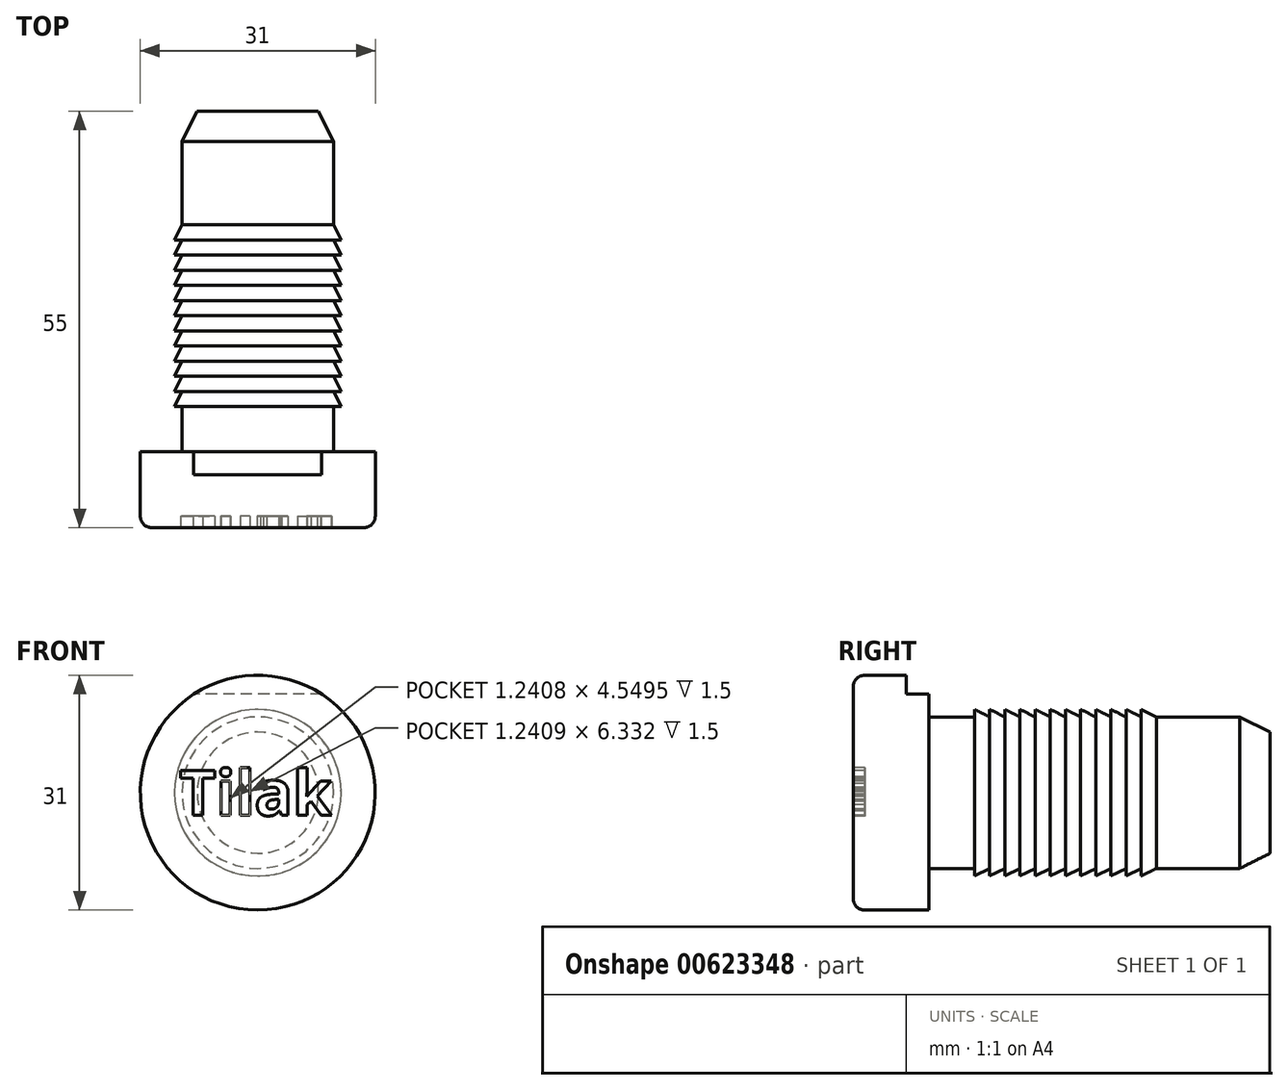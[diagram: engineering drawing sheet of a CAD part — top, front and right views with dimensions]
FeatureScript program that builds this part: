
annotation { "Feature Type Name" : "Feature", "Feature Type Description" : "" }
export const myFeature = defineFeature(function(context is Context, id is Id, definition is map)
    precondition{}
    {
        {
            var Q0;
            Q0=qCreatedBy(makeId("Front.planeOp"),FACE);
            var sketch = newSketch(context, id + "F0", { "sketchPlane" : qUnion([Q0])});
            skCircle(sketch, "E0", {"center": v(0, 0) * mm, "radius": 10 * mm});
            skSolve(sketch);
        }
        {
            var Q0;
            Q0 = qSketchRegion(id + "F0", true);
            extrude(context, id + "F1", {"entities" : qUnion([Q0]), "oppositeDirection" : true, "depth" : 45 * mm, "offsetDistance" : 25 * mm});
        }
        {
            var Q0;
            Q0=makeQuery(id+"F1.opExtrude","CAP_FACE",FACE,{"disambiguationData":[OSD([sQuery(id+"F0.wireOp",EDGE,"E0")])],"isStart":true});
            var sketch = newSketch(context, id + "F2", { "sketchPlane" : qUnion([Q0])});
            skCircle(sketch, "E1", {"center": v(0, 0) * mm, "radius": 15.5 * mm});
            skSolve(sketch);
        }
        {
            var Q0;
            Q0 = qSketchRegion(id + "F2", true);
            extrude(context, id + "F3", {"entities" : qUnion([Q0]), "operationType" : NewBodyOperationType.ADD, "depth" : 10 * mm, "offsetDistance" : 25 * mm});
        }
        {
            var Q0;
            Q0=makeQuery(id+"F3.opExtrude","CAP_FACE",FACE,{"disambiguationData":[OSD([sQuery(id+"F2.wireOp",EDGE,"E1")])],"isStart":true});
            var sketch = newSketch(context, id + "F4", { "sketchPlane" : qUnion([Q0])});
            skLineSegment(sketch, "E2", {"start": v(-8.44, 13) * mm, "end": v(8.44, 13) * mm});
            skCircle(sketch, "E3", {"center": v(0, 0) * mm, "radius": 10 * mm, "construction": true});
            skArc(sketch, "E4", {"start": v(-8.44, 13) * mm, "mid": v(0, 15.5) * mm, "end": v(8.44, 13) * mm});
            skSolve(sketch);
        }
        {
            var Q0;
            Q0 = qSketchRegion(id + "F4", true);
            extrude(context, id + "F5", {"entities" : qUnion([Q0]), "operationType" : NewBodyOperationType.REMOVE, "oppositeDirection" : true, "depth" : 3 * mm, "offsetDistance" : 25 * mm});
        }
        {
            var Q0;
            Q0=qCreatedBy(makeId("Right.planeOp"),FACE);
            var sketch = newSketch(context, id + "F6", { "sketchPlane" : qUnion([Q0])});
            skLineSegment(sketch, "E5.0", {"start": v(45, -10) * mm, "end": v(45, 10) * mm, "construction": true});
            skLineSegment(sketch, "E6", {"start": v(58.9, 0) * mm, "end": v(-32.08, 0) * mm, "construction": true});
            skLineSegment(sketch, "E7", {"start": v(30, 10) * mm, "end": v(28, 11) * mm});
            skLineSegment(sketch, "E8", {"start": v(28, 11) * mm, "end": v(28, 10) * mm});
            skLineSegment(sketch, "E9", {"start": v(28, 10) * mm, "end": v(30, 10) * mm});
            skLineSegment(sketch, "E10.0", {"start": v(0, -10) * mm, "end": v(0, 10) * mm, "construction": true});
            skLineSegment(sketch, "E11.1.0.0", {"start": v(26, 10) * mm, "end": v(28, 10) * mm});
            skLineSegment(sketch, "E11.1.0.1", {"start": v(26, 11) * mm, "end": v(26, 10) * mm});
            skLineSegment(sketch, "E11.1.0.2", {"start": v(28, 10) * mm, "end": v(26, 11) * mm});
            skLineSegment(sketch, "E11.2.0.0", {"start": v(24, 10) * mm, "end": v(26, 10) * mm});
            skLineSegment(sketch, "E11.2.0.1", {"start": v(24, 11) * mm, "end": v(24, 10) * mm});
            skLineSegment(sketch, "E11.2.0.2", {"start": v(26, 10) * mm, "end": v(24, 11) * mm});
            skLineSegment(sketch, "E11.3.0.0", {"start": v(22, 10) * mm, "end": v(24, 10) * mm});
            skLineSegment(sketch, "E11.3.0.1", {"start": v(22, 11) * mm, "end": v(22, 10) * mm});
            skLineSegment(sketch, "E11.3.0.2", {"start": v(24, 10) * mm, "end": v(22, 11) * mm});
            skLineSegment(sketch, "E11.4.0.0", {"start": v(20, 10) * mm, "end": v(22, 10) * mm});
            skLineSegment(sketch, "E11.4.0.1", {"start": v(20, 11) * mm, "end": v(20, 10) * mm});
            skLineSegment(sketch, "E11.4.0.2", {"start": v(22, 10) * mm, "end": v(20, 11) * mm});
            skLineSegment(sketch, "E11.5.0.0", {"start": v(18, 10) * mm, "end": v(20, 10) * mm});
            skLineSegment(sketch, "E11.5.0.1", {"start": v(18, 11) * mm, "end": v(18, 10) * mm});
            skLineSegment(sketch, "E11.5.0.2", {"start": v(20, 10) * mm, "end": v(18, 11) * mm});
            skLineSegment(sketch, "E11.6.0.0", {"start": v(16, 10) * mm, "end": v(18, 10) * mm});
            skLineSegment(sketch, "E11.6.0.1", {"start": v(16, 11) * mm, "end": v(16, 10) * mm});
            skLineSegment(sketch, "E11.6.0.2", {"start": v(18, 10) * mm, "end": v(16, 11) * mm});
            skLineSegment(sketch, "E11.7.0.0", {"start": v(14, 10) * mm, "end": v(16, 10) * mm});
            skLineSegment(sketch, "E11.7.0.1", {"start": v(14, 11) * mm, "end": v(14, 10) * mm});
            skLineSegment(sketch, "E11.7.0.2", {"start": v(16, 10) * mm, "end": v(14, 11) * mm});
            skLineSegment(sketch, "E11.8.0.0", {"start": v(12, 10) * mm, "end": v(14, 10) * mm});
            skLineSegment(sketch, "E11.8.0.1", {"start": v(12, 11) * mm, "end": v(12, 10) * mm});
            skLineSegment(sketch, "E11.8.0.2", {"start": v(14, 10) * mm, "end": v(12, 11) * mm});
            skLineSegment(sketch, "E11.9.0.0", {"start": v(10, 10) * mm, "end": v(12, 10) * mm});
            skLineSegment(sketch, "E11.9.0.1", {"start": v(10, 11) * mm, "end": v(10, 10) * mm});
            skLineSegment(sketch, "E11.9.0.2", {"start": v(12, 10) * mm, "end": v(10, 11) * mm});
            skLineSegment(sketch, "E11.10.0.0", {"start": v(8, 10) * mm, "end": v(10, 10) * mm});
            skLineSegment(sketch, "E11.10.0.1", {"start": v(8, 11) * mm, "end": v(8, 10) * mm});
            skLineSegment(sketch, "E11.10.0.2", {"start": v(10, 10) * mm, "end": v(8, 11) * mm});
            skLineSegment(sketch, "E11.11.0.0", {"start": v(6, 10) * mm, "end": v(8, 10) * mm});
            skLineSegment(sketch, "E11.11.0.1", {"start": v(6, 11) * mm, "end": v(6, 10) * mm});
            skLineSegment(sketch, "E11.11.0.2", {"start": v(8, 10) * mm, "end": v(6, 11) * mm});
            skLineSegment(sketch, "E11.direction1", {"start": v(28, 10) * mm, "end": v(26, 10) * mm, "construction": true});
            skSolve(sketch);
        }
        {
            var Q0;
            Q0 = qSketchRegion(id + "F6", true);
            var Q1;
            Q1=sQuery(id+"F6.wireOp",EDGE,"E6");
            revolve(context, id + "F7", {"operationType" : NewBodyOperationType.ADD, "entities" : qUnion([Q0]), "axis" : qUnion([Q1]), "revolveType" : RevolveType.FULL});
        }
        {
            var Q0;
            Q0=makeQuery(id+"F1.opExtrude","CAP_FACE",FACE,{"disambiguationData":[OSD([sQuery(id+"F0.wireOp",EDGE,"E0")])],"isStart":false});
            chamfer(context, id + "F8", {"entities" : qUnion([Q0]), "chamferType" : ChamferType.TWO_OFFSETS, "width1" : 4 * mm, "oppositeDirection" : false, "width2" : 2 * mm, "tangentPropagation" : true});
        }
        {
            var Q0;
            Q0=makeQuery(id+"F1.opExtrude","CAP_EDGE",EDGE,{"disambiguationData":[OSD([sQuery(id+"F0.wireOp",EDGE,"E0")])],"isStart":true});
            var Q1;
            Q1=makeQuery(id+"F3.opExtrude","CAP_EDGE",EDGE,{"disambiguationData":[OSD([sQuery(id+"F2.wireOp",EDGE,"E1")])],"isStart":false});
            fillet(context, id + "F9", {"entities" : qUnion([Q0, Q1]), "radius" : 1.5 * mm, "tangentPropagation" : true, "allowEdgeOverflow" : false});
        }
        {
            var Q0;
            Q0=makeQuery(id+"F3.opExtrude","CAP_FACE",FACE,{"disambiguationData":[OSD([sQuery(id+"F2.wireOp",EDGE,"E1")])],"isStart":false});
            var sketch = newSketch(context, id + "F10", { "sketchPlane" : qUnion([Q0])});
            skText(sketch, "E12", { "text": "Tilak", "fontName": "OpenSans-Bold.ttf"});
            skLineSegment(sketch, "E13", {"start": v(-17.1, 0) * mm, "end": v(36.8, 0) * mm, "construction": true});
            const initialGuessF10  = {"E12": [-0.01033, -0.003, 1, 0, 0.006]};
            skSetInitialGuess(sketch, initialGuessF10);
            skSolve(sketch);
        }
        {
            var Q0;
            Q0 = qSketchRegion(id + "F10", true);
            extrude(context, id + "F11", {"entities" : qUnion([Q0]), "operationType" : NewBodyOperationType.REMOVE, "oppositeDirection" : true, "depth" : 1.5 * mm, "offsetDistance" : 25 * mm});
        }
    });
